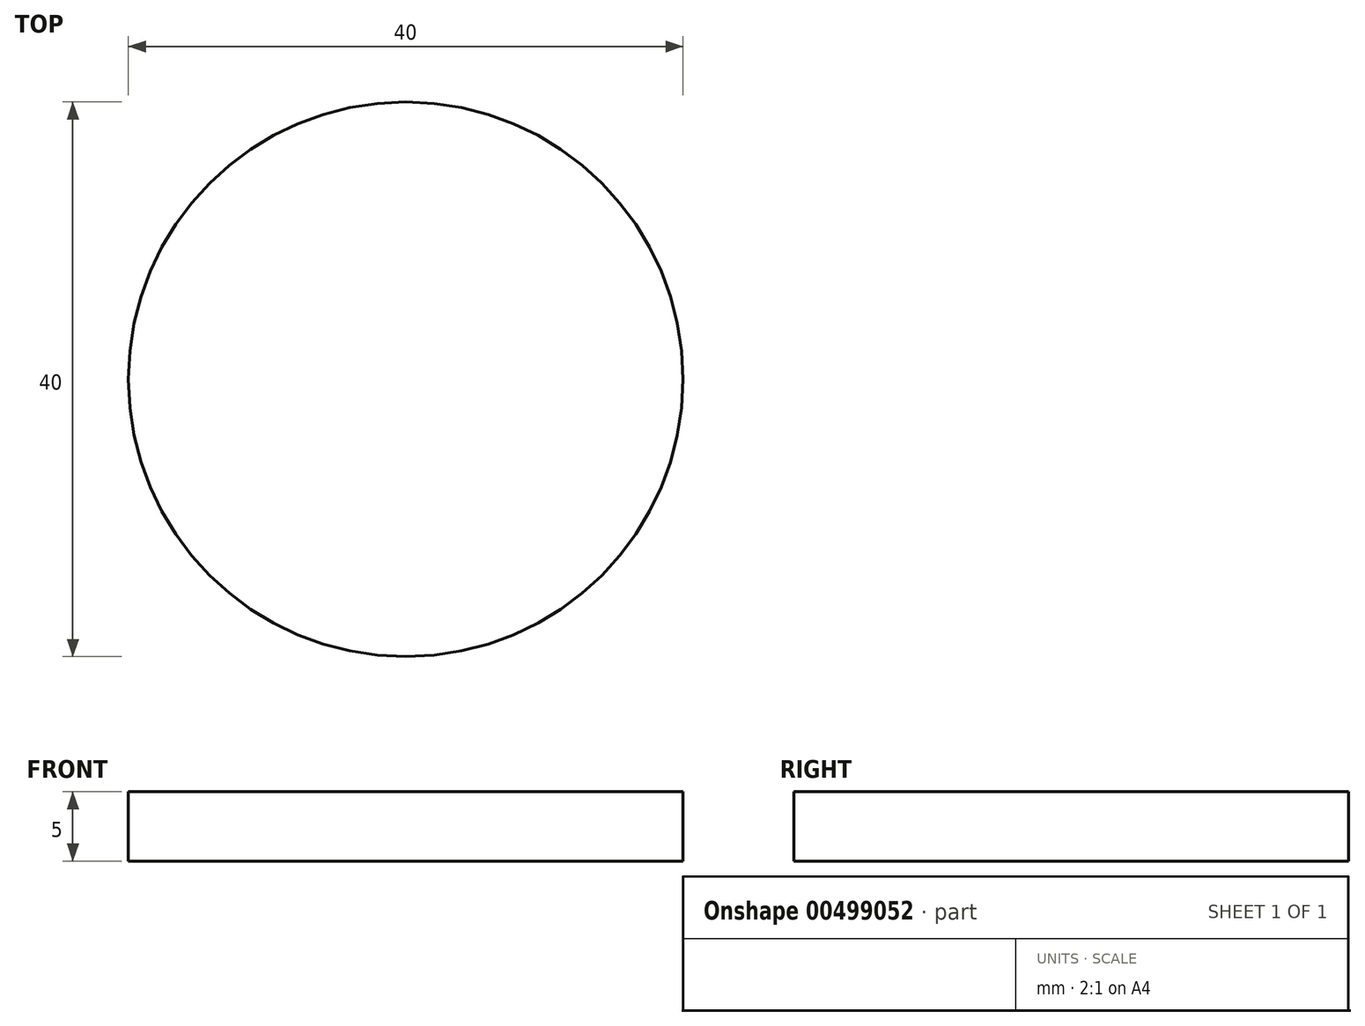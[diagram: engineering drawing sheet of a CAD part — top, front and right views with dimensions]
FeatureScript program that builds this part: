
annotation { "Feature Type Name" : "Feature", "Feature Type Description" : "" }
export const myFeature = defineFeature(function(context is Context, id is Id, definition is map)
    precondition{}
    {
        {
            var Q0;
            Q0=qCreatedBy(makeId("Top.planeOp"),FACE);
            var sketch = newSketch(context, id + "F0", { "sketchPlane" : qUnion([Q0])});
            skCircle(sketch, "E0", {"center": v(0, 0) * mm, "radius": 20 * mm});
            skSolve(sketch);
        }
        {
            var Q0;
            Q0 = qSketchRegion(id + "F0", true);
            extrude(context, id + "F1", {"entities" : qUnion([Q0]), "depth" : 5 * mm});
        }
    });
